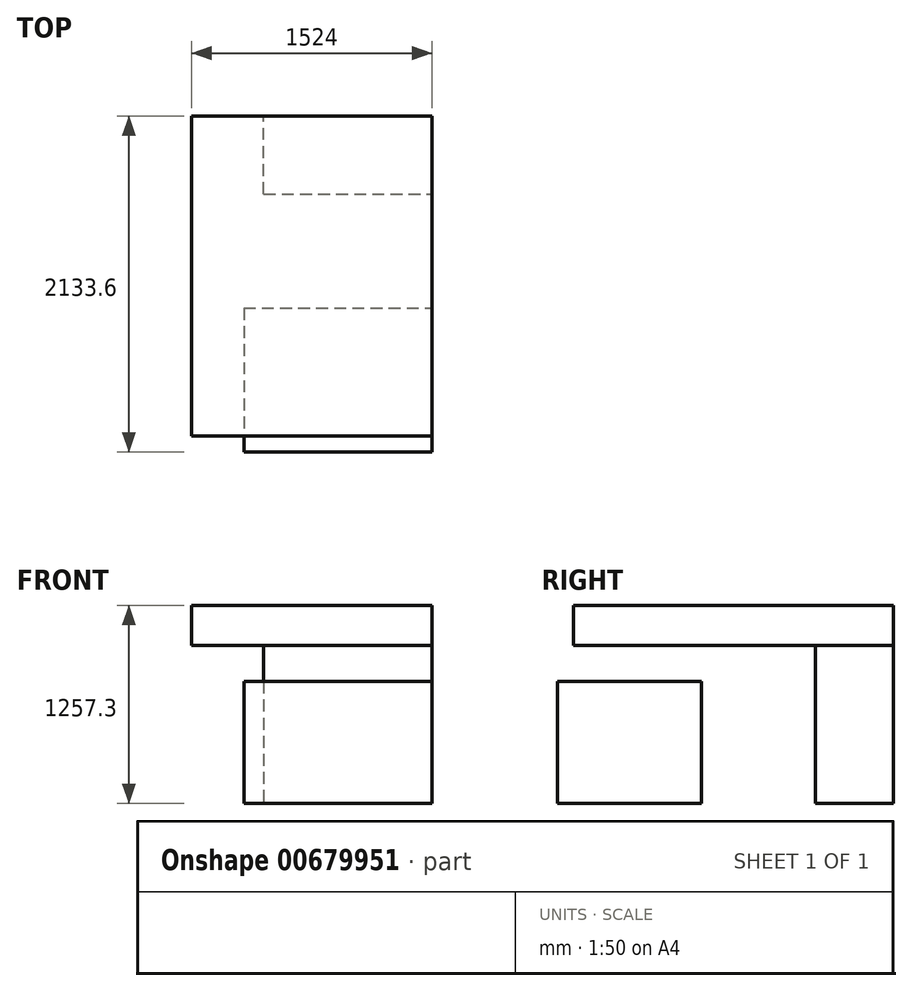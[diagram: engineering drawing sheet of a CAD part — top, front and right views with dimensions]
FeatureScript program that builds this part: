
annotation { "Feature Type Name" : "Feature", "Feature Type Description" : "" }
export const myFeature = defineFeature(function(context is Context, id is Id, definition is map)
    precondition{}
    {
        {
            var Q0;
            Q0=qCreatedBy(makeId("Top.planeOp"),FACE);
            var sketch = newSketch(context, id + "F0", { "sketchPlane" : qUnion([Q0])});
            skLineSegment(sketch, "E0.bottom", {"start": v(-701.98, 893.89) * mm, "end": v(822.02, 893.89) * mm});
            skLineSegment(sketch, "E0.top", {"start": v(-701.98, -1239.71) * mm, "end": v(822.02, -1239.71) * mm});
            skLineSegment(sketch, "E0.left", {"start": v(-701.98, 893.89) * mm, "end": v(-701.98, -1239.71) * mm});
            skLineSegment(sketch, "E0.right", {"start": v(822.02, 893.89) * mm, "end": v(822.02, -1239.71) * mm});
            skSolve(sketch);
        }
        {
            var Q0;
            Q0=qCreatedBy(makeId("Top.planeOp"),FACE);
            var sketch = newSketch(context, id + "F1", { "sketchPlane" : qUnion([Q0])});
            skLineSegment(sketch, "E1.bottom", {"start": v(-274.17, -251.14) * mm, "end": v(792.63, -251.14) * mm});
            skLineSegment(sketch, "E1.top", {"start": v(-274.17, 244.16) * mm, "end": v(792.63, 244.16) * mm});
            skLineSegment(sketch, "E1.left", {"start": v(-274.17, -251.14) * mm, "end": v(-274.17, 244.16) * mm});
            skLineSegment(sketch, "E1.right", {"start": v(792.63, -251.14) * mm, "end": v(792.63, 244.16) * mm});
            skSolve(sketch);
        }
        {
            var Q0;
            Q0 = qSketchRegion(id + "F1", true);
            extrude(context, id + "F2", {"entities" : qUnion([Q0]), "depth" : 1003.3 * mm, "offsetDistance" : 25.4 * mm});
        }
        {
            var Q0;
            Q0=qCreatedBy(makeId("Top.planeOp"),FACE);
            var sketch = newSketch(context, id + "F3", { "sketchPlane" : qUnion([Q0])});
            skLineSegment(sketch, "E2.bottom", {"start": v(-268.72, -375.89) * mm, "end": v(925.08, -375.89) * mm});
            skLineSegment(sketch, "E2.top", {"start": v(-268.72, -1290.29) * mm, "end": v(925.08, -1290.29) * mm});
            skLineSegment(sketch, "E2.left", {"start": v(-268.72, -375.89) * mm, "end": v(-268.72, -1290.29) * mm});
            skLineSegment(sketch, "E2.right", {"start": v(925.08, -375.89) * mm, "end": v(925.08, -1290.29) * mm});
            skSolve(sketch);
        }
        {
            var Q0;
            Q0 = qSketchRegion(id + "F3", true);
            extrude(context, id + "F4", {"entities" : qUnion([Q0]), "depth" : 774.7 * mm, "offsetDistance" : 25.4 * mm});
        }
        {
            var Q0;
            Q0=makeQuery(id+"F0.imprint","IMPRINT",FACE,{"disambiguationData":[TD([[makeQuery(id+"F0.imprint","IMPRINT",EDGE,{"derivedFrom":sQuery(id+"F0.wireOp",EDGE,"E0.bottom")}),-1.0]])]});
            var sketch = newSketch(context, id + "F5", { "sketchPlane" : qUnion([Q0])});
            skLineSegment(sketch, "E3.bottom", {"start": v(-2356.26, -632.11) * mm, "end": v(-832.26, -632.11) * mm});
            skLineSegment(sketch, "E3.top", {"start": v(-2356.26, -2664.11) * mm, "end": v(-832.26, -2664.11) * mm});
            skLineSegment(sketch, "E3.left", {"start": v(-2356.26, -632.11) * mm, "end": v(-2356.26, -2664.11) * mm});
            skLineSegment(sketch, "E3.right", {"start": v(-832.26, -632.11) * mm, "end": v(-832.26, -2664.11) * mm});
            skSolve(sketch);
        }
        {
            var Q0;
            Q0=makeQuery(id+"F5.imprint","IMPRINT",FACE,{"disambiguationData":[TD([[makeQuery(id+"F5.imprint","IMPRINT",EDGE,{"derivedFrom":sQuery(id+"F5.wireOp",EDGE,"E3.bottom")}),-1.0]])]});
            extrude(context, id + "F6", {"entities" : qUnion([Q0]), "depth" : 254 * mm, "offsetDistance" : 25.4 * mm});
        }
        {
            var Q0;
            Q0=makeQuery(id+"F2.opExtrude","SWEPT_BODY",BODY,{"disambiguationData":[OSD([sQuery(id+"F1.wireOp",EDGE,"E1.bottom"),sQuery(id+"F1.wireOp",EDGE,"E1.top"),sQuery(id+"F1.wireOp",EDGE,"E1.left"),sQuery(id+"F1.wireOp",EDGE,"E1.right")])]});
            var Q1;
            Q1=makeQuery(id+"F2.opExtrude","CAP_VERTEX",VERTEX,{"disambiguationData":[OSD([sQuery(id+"F1.wireOp",EDGE,"E1.top"),sQuery(id+"F1.wireOp",EDGE,"E1.right")])],"isStart":true});
            var Q2;
            Q2=sQuery(id+"F0.wireOp",VERTEX,"E0.right.start");
            transform(context, id + "F7", {"entities" : qUnion([Q0]), "transformType" : TransformType.TRANSLATION_ENTITY, "oppositeDirectionEntity" : false, "transformLine" : qUnion([Q1, Q2]), "makeCopy" : false});
        }
        {
            var Q0;
            Q0=makeQuery(id+"F4.opExtrude","SWEPT_BODY",BODY,{"disambiguationData":[OSD([sQuery(id+"F3.wireOp",EDGE,"E2.bottom"),sQuery(id+"F3.wireOp",EDGE,"E2.top"),sQuery(id+"F3.wireOp",EDGE,"E2.left"),sQuery(id+"F3.wireOp",EDGE,"E2.right")])]});
            var Q1;
            Q1=makeQuery(id+"F4.opExtrude","CAP_VERTEX",VERTEX,{"disambiguationData":[OSD([sQuery(id+"F3.wireOp",EDGE,"E2.top"),sQuery(id+"F3.wireOp",EDGE,"E2.right")])],"isStart":true});
            var Q2;
            Q2=sQuery(id+"F0.wireOp",VERTEX,"E0.right.end");
            transform(context, id + "F8", {"entities" : qUnion([Q0]), "transformType" : TransformType.TRANSLATION_ENTITY, "oppositeDirectionEntity" : false, "transformLine" : qUnion([Q1, Q2]), "makeCopy" : false});
        }
        {
            var Q0;
            Q0=makeQuery(id+"F6.opExtrude","SWEPT_BODY",BODY,{"disambiguationData":[OSD([sQuery(id+"F5.wireOp",EDGE,"E3.bottom"),sQuery(id+"F5.wireOp",EDGE,"E3.top"),sQuery(id+"F5.wireOp",EDGE,"E3.left"),sQuery(id+"F5.wireOp",EDGE,"E3.right")])]});
            var Q1;
            Q1=makeQuery(id+"F6.opExtrude","CAP_VERTEX",VERTEX,{"disambiguationData":[OSD([sQuery(id+"F5.wireOp",EDGE,"E3.bottom"),sQuery(id+"F5.wireOp",EDGE,"E3.right")])],"isStart":true});
            var Q2;
            Q2=makeQuery(id+"F2.opExtrude","CAP_VERTEX",VERTEX,{"disambiguationData":[OSD([sQuery(id+"F1.wireOp",EDGE,"E1.top"),sQuery(id+"F1.wireOp",EDGE,"E1.right")])],"isStart":false});
            transform(context, id + "F9", {"entities" : qUnion([Q0]), "transformType" : TransformType.TRANSLATION_ENTITY, "oppositeDirectionEntity" : false, "transformLine" : qUnion([Q1, Q2]), "makeCopy" : false});
        }
    });
